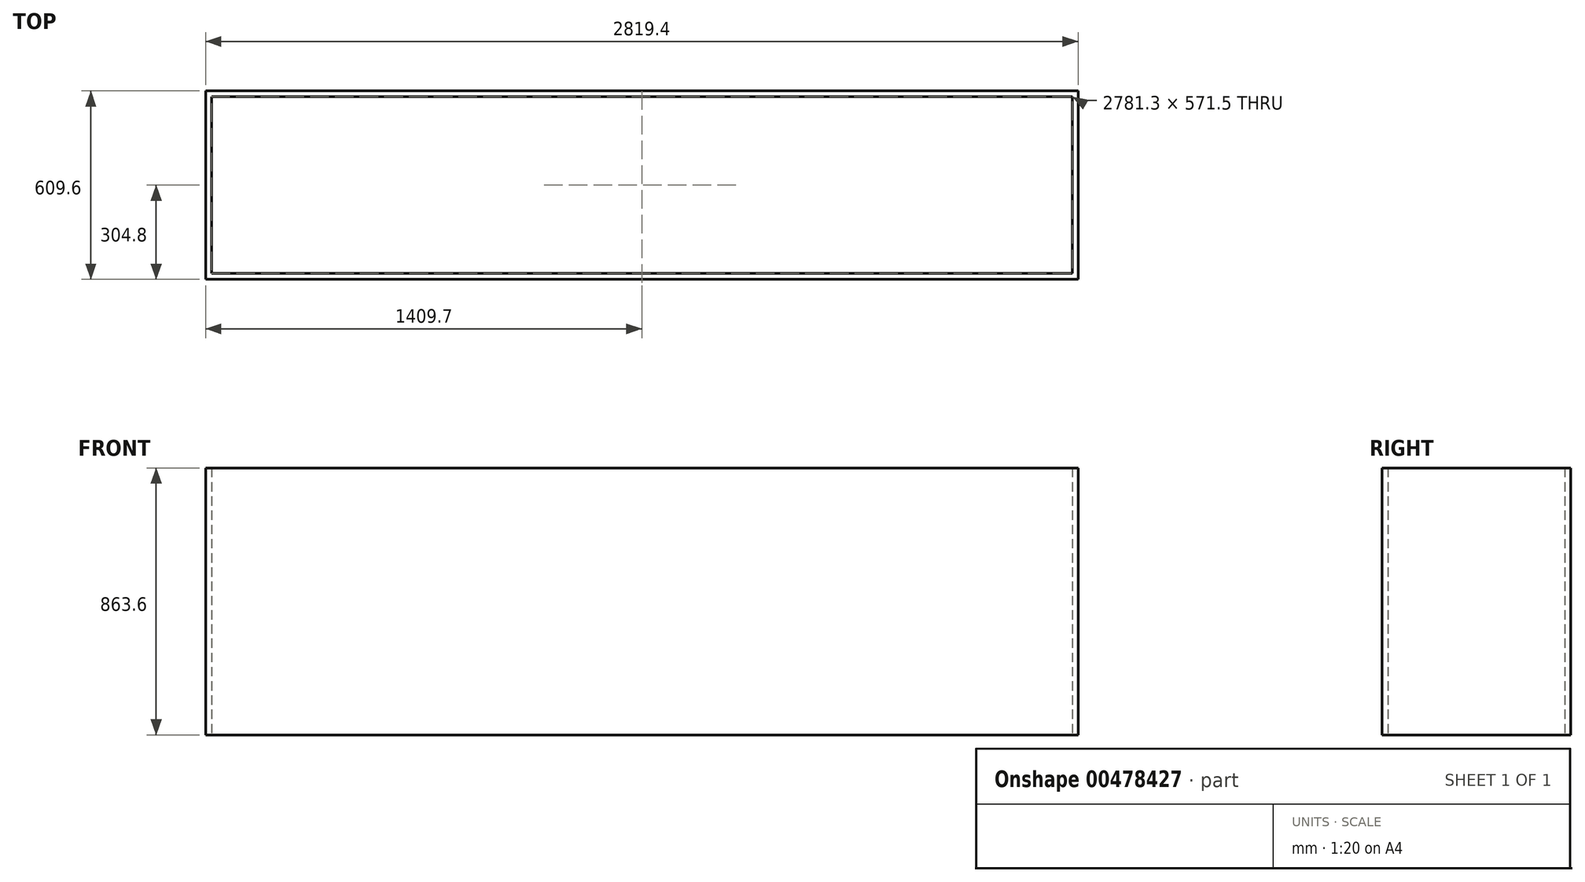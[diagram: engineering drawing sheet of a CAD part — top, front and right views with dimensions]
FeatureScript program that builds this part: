
annotation { "Feature Type Name" : "Feature", "Feature Type Description" : "" }
export const myFeature = defineFeature(function(context is Context, id is Id, definition is map)
    precondition{}
    {
        {
            var Q0;
            Q0=qCreatedBy(makeId("Top.planeOp"),FACE);
            var sketch = newSketch(context, id + "F0", { "sketchPlane" : qUnion([Q0])});
            skLineSegment(sketch, "E0.bottom", {"start": v(0, 0) * mm, "end": v(0, 0) * mm});
            skLineSegment(sketch, "E0.top", {"start": v(0, 0) * mm, "end": v(0, 0) * mm});
            skLineSegment(sketch, "E0.left", {"start": v(0, 0) * mm, "end": v(0, 0) * mm});
            skLineSegment(sketch, "E0.right", {"start": v(0, 0) * mm, "end": v(0, 0) * mm});
            skPoint(sketch, "E0.middle", {"position": v(0, 0) * mm});
            skLineSegment(sketch, "E1.bottom", {"start": v(1409.7, 304.8) * mm, "end": v(-1409.7, 304.8) * mm});
            skLineSegment(sketch, "E1.top", {"start": v(1409.7, -304.8) * mm, "end": v(-1409.7, -304.8) * mm});
            skLineSegment(sketch, "E1.left", {"start": v(1409.7, 304.8) * mm, "end": v(1409.7, -304.8) * mm});
            skLineSegment(sketch, "E1.right", {"start": v(-1409.7, 304.8) * mm, "end": v(-1409.7, -304.8) * mm});
            skSolve(sketch);
        }
        {
            var Q0;
            Q0=makeQuery(id+"F0.imprint","IMPRINT",FACE,{"disambiguationData":[TD([[makeQuery(id+"F0.imprint","IMPRINT",EDGE,{"derivedFrom":sQuery(id+"F0.wireOp",EDGE,"E1.bottom")}),1.0]])]});
            var sketch = newSketch(context, id + "F1", { "sketchPlane" : qUnion([Q0])});
            skLineSegment(sketch, "E2.bottom", {"start": v(1390.65, 285.75) * mm, "end": v(-1390.65, 285.75) * mm});
            skLineSegment(sketch, "E2.top", {"start": v(1390.65, -285.75) * mm, "end": v(-1390.65, -285.75) * mm});
            skLineSegment(sketch, "E2.left", {"start": v(1390.65, 285.75) * mm, "end": v(1390.65, -285.75) * mm});
            skLineSegment(sketch, "E2.right", {"start": v(-1390.65, 285.75) * mm, "end": v(-1390.65, -285.75) * mm});
            skPoint(sketch, "E2.middle", {"position": v(0, 0) * mm});
            skSolve(sketch);
        }
        {
            var Q0;
            Q0=makeQuery(id+"F1.imprint","IMPRINT",FACE,{"disambiguationData":[TD([[makeQuery(id+"F1.imprint","IMPRINT",EDGE,{"derivedFrom":sQuery(id+"F1.wireOp",EDGE,"E2.bottom")}),-1.0]])]});
            extrude(context, id + "F2", {"entities" : qUnion([Q0]), "depth" : 863.6 * mm, "offsetDistance" : 25.4 * mm});
        }
    });
